# Revit family: MDF-U700VXC-PA
name_source: partatom
category: Mechanical Equipment
revit_build: Autodesk Revit MEP 2012 (Build: 20110309_2315(x64)
units: mm (PartAtom-declared; Revit-internal decimal feet)

## types (1)
- MDF-U700VXC-PA
    Actual Weight = 0
    Defrost Num Day = 0
    Defrost Termination = not applicable
    Defrost Type = not applicable
    Description = Ultra-Low Freezers - Upright, Twin Guard Series
    Door = Aluminum
    EQUIPMENT DESCRIPTION = =Description
    EQUIPMENT MARK = =Legend Number
    Evap Temp = -90
    Fridge = Aluminum
    Glass = Glass
    Handle = Aluminum
    Height = 6' - 7"
    LOAD 1 CLASSIFICATION = Power
    LOAD 1 DEDICATED CIRCUIT REQUIRED = Yes
    LOAD 1 DESCRIPTION = single phase 208/220V 60Hz
    LOAD 1 ENERGY SETBACK REQUIRED = No
    LOAD 1 GROUND FAULT PROTECTION REQUIRED = No
    LOAD 1 ISOLATED GROUND REQUIRED = No
    LOAD 1 MOUNTING HEIGHT ABOVE FLOOR = 0' - 4"
    LOAD 1 NEUTRAL REQUIRED = Yes
    LOAD 1 PLUG TYPE = Nema 6-15P
    LOAD 1 POLES = 1
    LOAD 1 VOLTAGE = 208 V
    LOAD 1 WATTAGE = 1100 W
    Legend Number = Millimeters
    Legs = Yes
    Length = 2' - 10 1/2"
    Load Mbh = 5743
    Manufacturer = Panasonic
    Model = Panasonic MDF-U700VXC-PA
    Panel = Plastic
    Refrig Charge Lbs = MU-N700. 475g
    Shelves = Metal Shelf
    Supplier = Panasonic Healthcare Company of North America
Panasonic Healthcare Company of North America
    Supplier Model = MDF-U700VXC-PA
    Switch = Switch
    URL = http://us.sanyo.com
    Vents = Metal Steel
    Wheel = Stainless Steel
    Wheels = Yes
    Width = 3' - 4"

## geometry (parser evidence)
native form markers: Blend x26, Sweep x18
no freeform markers — native parametric forms only
